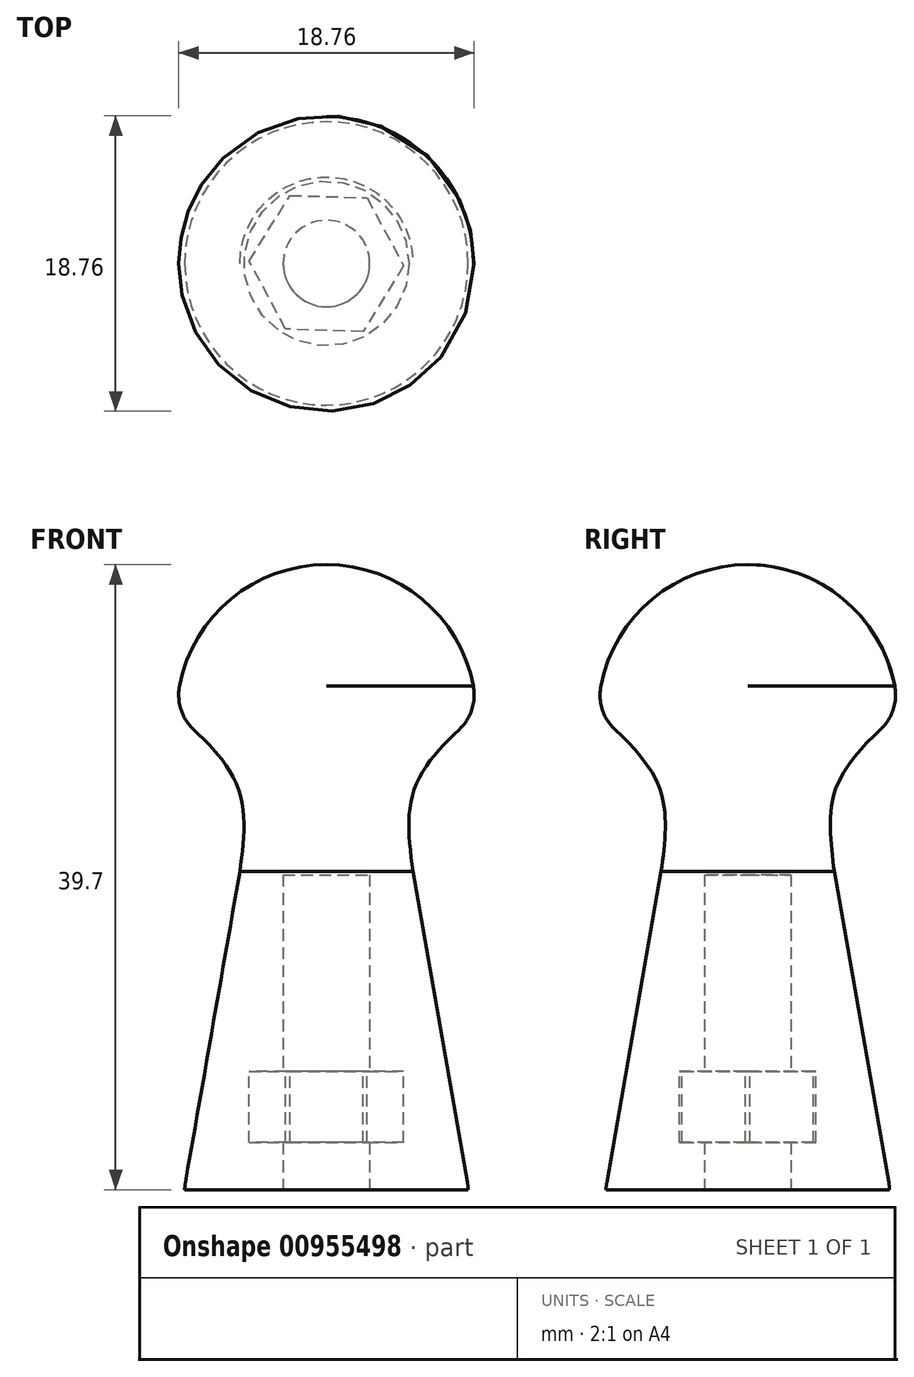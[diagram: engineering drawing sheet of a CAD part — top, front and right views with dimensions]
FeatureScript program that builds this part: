
annotation { "Feature Type Name" : "Feature", "Feature Type Description" : "" }
export const myFeature = defineFeature(function(context is Context, id is Id, definition is map)
    precondition{}
    {
        {
            var Q0;
            Q0=qCreatedBy(makeId("Top.planeOp"),FACE);
            var sketch = newSketch(context, id + "F0", { "sketchPlane" : qUnion([Q0])});
            skCircle(sketch, "E0", {"center": v(0, 0) * mm, "radius": 9 * mm});
            skSolve(sketch);
        }
        {
            var Q0;
            Q0=makeQuery(id+"F0.imprint","IMPRINT",FACE,{"disambiguationData":[TD([[makeQuery(id+"F0.imprint","IMPRINT",EDGE,{"derivedFrom":sQuery(id+"F0.wireOp",EDGE,"E0")}),1.0]])]});
            var Q1;
            Q1=sQuery(id+"F0.wireOp",EDGE,"E0");
            extrude(context, id + "F1", {"entities" : qUnion([Q0]), "surfaceEntities" : qUnion([Q1]), "depth" : .2 * mm, "offsetDistance" : 25 * mm});
        }
        {
            var Q0;
            Q0=makeQuery(id+"F1.opExtrude","CAP_FACE",FACE,{"disambiguationData":[OSD([sQuery(id+"F0.wireOp",EDGE,"E0")])],"isStart":false});
            cPlane(context, id + "F2", {"entities" : qUnion([Q0]), "cplaneType" : CPlaneType.OFFSET, "offset" : 20 * mm, "width" : 150 * mm, "height" : 150 * mm});
        }
        {
            var Q0;
            Q0=qCreatedBy(id+"F2.planeOp",FACE);
            var sketch = newSketch(context, id + "F3", { "sketchPlane" : qUnion([Q0])});
            skCircle(sketch, "E1", {"center": v(0, 0) * mm, "radius": 5.5 * mm});
            skSolve(sketch);
        }
        {
            var Q0;
            Q0=makeQuery(id+"F3.imprint","IMPRINT",FACE,{"disambiguationData":[TD([[makeQuery(id+"F3.imprint","IMPRINT",EDGE,{"derivedFrom":sQuery(id+"F3.wireOp",EDGE,"E1")}),1.0]])]});
            cPlane(context, id + "F4", {"entities" : qUnion([Q0]), "cplaneType" : CPlaneType.OFFSET, "offset" : 5 * mm, "width" : 150 * mm, "height" : 150 * mm});
        }
        {
            var Q0;
            Q0=qCreatedBy(id+"F4.planeOp",FACE);
            var sketch = newSketch(context, id + "F5", { "sketchPlane" : qUnion([Q0])});
            skCircle(sketch, "E2", {"center": v(0, 0) * mm, "radius": 5.5 * mm});
            skSolve(sketch);
        }
        {
            var Q0;
            Q0=qCreatedBy(id+"F4.planeOp",FACE);
            cPlane(context, id + "F6", {"entities" : qUnion([Q0]), "cplaneType" : CPlaneType.OFFSET, "offset" : 5 * mm, "width" : 150 * mm, "height" : 150 * mm});
        }
        {
            var Q0;
            Q0=qCreatedBy(id+"F6.planeOp",FACE);
            var sketch = newSketch(context, id + "F7", { "sketchPlane" : qUnion([Q0])});
            skCircle(sketch, "E3", {"center": v(0, 0) * mm, "radius": 9.5 * mm});
            skSolve(sketch);
        }
        {
            var Q1;
            Q1=makeQuery(id+"F1.opExtrude","CAP_FACE",FACE,{"disambiguationData":[OSD([sQuery(id+"F0.wireOp",EDGE,"E0")])],"isStart":false});
            var Q2;
            Q2=makeQuery(id+"F3.imprint","IMPRINT",FACE,{"disambiguationData":[TD([[makeQuery(id+"F3.imprint","IMPRINT",EDGE,{"derivedFrom":sQuery(id+"F3.wireOp",EDGE,"E1")}),1.0]])]});
            loft(context, id + "F8", {"operationType" : NewBodyOperationType.ADD, "sheetProfilesArray" : [{ "sheetProfileEntities" : qUnion([Q1]) }, { "sheetProfileEntities" : qUnion([Q2]) }]});
        }
        {
            var Q0;
            Q0=makeQuery(id+"F3.imprint","IMPRINT",FACE,{"disambiguationData":[TD([[makeQuery(id+"F3.imprint","IMPRINT",EDGE,{"derivedFrom":sQuery(id+"F3.wireOp",EDGE,"E1")}),1.0]])]});
            var Q1;
            Q1=makeQuery(id+"F5.imprint","IMPRINT",FACE,{"disambiguationData":[TD([[makeQuery(id+"F5.imprint","IMPRINT",EDGE,{"derivedFrom":sQuery(id+"F5.wireOp",EDGE,"E2")}),1.0]])]});
            var Q2;
            Q2=makeQuery(id+"F7.imprint","IMPRINT",FACE,{"disambiguationData":[TD([[makeQuery(id+"F7.imprint","IMPRINT",EDGE,{"derivedFrom":sQuery(id+"F7.wireOp",EDGE,"E3")}),1.0]])]});
            loft(context, id + "F9", {"operationType" : NewBodyOperationType.ADD, "sheetProfilesArray" : [{ "sheetProfileEntities" : qUnion([Q0]) }, { "sheetProfileEntities" : qUnion([Q1]) }, { "sheetProfileEntities" : qUnion([Q2]) }]});
        }
        {
            var Q0;
            Q0=qCreatedBy(makeId("Right.planeOp"),FACE);
            var sketch = newSketch(context, id + "F10", { "sketchPlane" : qUnion([Q0])});
            skPoint(sketch, "E4", {"position": v(0, 30.2) * mm});
            skArc(sketch, "E5", {"start": v(9.5, 30.2) * mm, "mid": v(6.72, 36.92) * mm, "end": v(0, 39.7) * mm});
            skLineSegment(sketch, "E6", {"start": v(0, 39.7) * mm, "end": v(0, 30.2) * mm});
            skFitSpline(sketch, "E7.0.0", {"points": [v(-9.5, 40) * mm, v(-3.17, 40) * mm, v(3.17, 40) * mm, v(9.5, 40) * mm], "construction": true});
            skLineSegment(sketch, "E8", {"start": v(0, 30.2) * mm, "end": v(9.5, 30.2) * mm});
            skSolve(sketch);
        }
        {
            var Q0;
            Q0=makeQuery(id+"F10.imprint","IMPRINT",FACE,{"disambiguationData":[TD([[makeQuery(id+"F10.imprint","IMPRINT",EDGE,{"derivedFrom":sQuery(id+"F10.wireOp",EDGE,"E5")}),1.0]])]});
            var Q1;
            Q1=sQuery(id+"F10.wireOp",EDGE,"E6");
            revolve(context, id + "F11", {"operationType" : NewBodyOperationType.ADD, "surfaceOperationType" : NewSurfaceOperationType.NEW, "entities" : qUnion([Q0]), "axis" : qUnion([Q1]), "revolveType" : RevolveType.FULL});
        }
        {
            var Q0;
            Q0=makeQuery(id+"F11.boolean.opBoolean","MERGE",EDGE,{"derivedFrom":[makeQuery(id+"F9.opLoft","MID_CAP_EDGE",EDGE,{"disambiguationData":[OSD([sQuery(id+"F7.wireOp",EDGE,"E3")])],"capPos":2.0}),makeQuery(id+"F11.opRevolve","SWEPT_EDGE",EDGE,{"disambiguationData":[OSD([sQuery(id+"F10.wireOp",EDGE,"E5"),sQuery(id+"F10.wireOp",EDGE,"E8")])]})]});
            var Q1;
            {var subQ0=sQuery(id+"F0.wireOp",EDGE,"E0");Q1=makeQuery(id+"F8.boolean.opBoolean","MERGE",EDGE,{"derivedFrom":[makeQuery(id+"F1.opExtrude","CAP_EDGE",EDGE,{"disambiguationData":[OSD([subQ0])],"isStart":false}),makeQuery(id+"F8.opLoft","MID_CAP_EDGE",EDGE,{"disambiguationData":[OSD([subQ0])],"capPos":0.0})]});}
            fillet(context, id + "F12", {"entities" : qUnion([Q0, Q1]), "radius" : 3 * mm, "allowEdgeOverflow" : false});
        }
        {
            var Q0;
            Q0=qCreatedBy(makeId("Top.planeOp"),FACE);
            cPlane(context, id + "F13", {"entities" : qUnion([Q0]), "cplaneType" : CPlaneType.OFFSET, "offset" : 7.5 * mm, "width" : 150 * mm, "height" : 150 * mm});
        }
        {
            var Q0;
            Q0=qCreatedBy(id+"F13.planeOp",FACE);
            var sketch = newSketch(context, id + "F14", { "sketchPlane" : qUnion([Q0])});
            skCircle(sketch, "E9.cCircle", {"center": v(0, 0) * mm, "radius": 4.25 * mm, "construction": true});
            skLineSegment(sketch, "E9.0", {"start": v(-2.58, -4.17) * mm, "end": v(-4.9, 0.15) * mm});
            skLineSegment(sketch, "E9.1", {"start": v(-4.9, 0.15) * mm, "end": v(-2.32, 4.32) * mm});
            skLineSegment(sketch, "E9.2", {"start": v(-2.32, 4.32) * mm, "end": v(2.58, 4.17) * mm});
            skLineSegment(sketch, "E9.3", {"start": v(2.58, 4.17) * mm, "end": v(4.9, -0.15) * mm});
            skLineSegment(sketch, "E9.4", {"start": v(4.9, -0.15) * mm, "end": v(2.32, -4.32) * mm});
            skLineSegment(sketch, "E9.5", {"start": v(2.32, -4.32) * mm, "end": v(-2.58, -4.17) * mm});
            skPoint(sketch, "E9.0.midPoint", {"position": v(-3.74, -2.01) * mm});
            skSolve(sketch);
        }
        {
            var Q0;
            Q0 = qSketchRegion(id + "F14", true);
            extrude(context, id + "F15", {"entities" : qUnion([Q0]), "operationType" : NewBodyOperationType.REMOVE, "oppositeDirection" : true, "depth" : 4.5 * mm, "offsetDistance" : 25 * mm});
        }
        {
            var Q0;
            Q0=makeQuery(id+"F1.opExtrude","CAP_FACE",FACE,{"disambiguationData":[OSD([sQuery(id+"F0.wireOp",EDGE,"E0")])],"isStart":true});
            var sketch = newSketch(context, id + "F16", { "sketchPlane" : qUnion([Q0])});
            skCircle(sketch, "E10", {"center": v(0, 0) * mm, "radius": 2.75 * mm});
            skSolve(sketch);
        }
        {
            var Q0;
            Q0=makeQuery(id+"F16.imprint","IMPRINT",FACE,{"disambiguationData":[TD([[makeQuery(id+"F16.imprint","IMPRINT",EDGE,{"derivedFrom":sQuery(id+"F16.wireOp",EDGE,"E10")}),1.0]])]});
            extrude(context, id + "F17", {"entities" : qUnion([Q0]), "operationType" : NewBodyOperationType.REMOVE, "oppositeDirection" : true, "depth" : 20 * mm, "offsetDistance" : 25 * mm});
        }
    });
